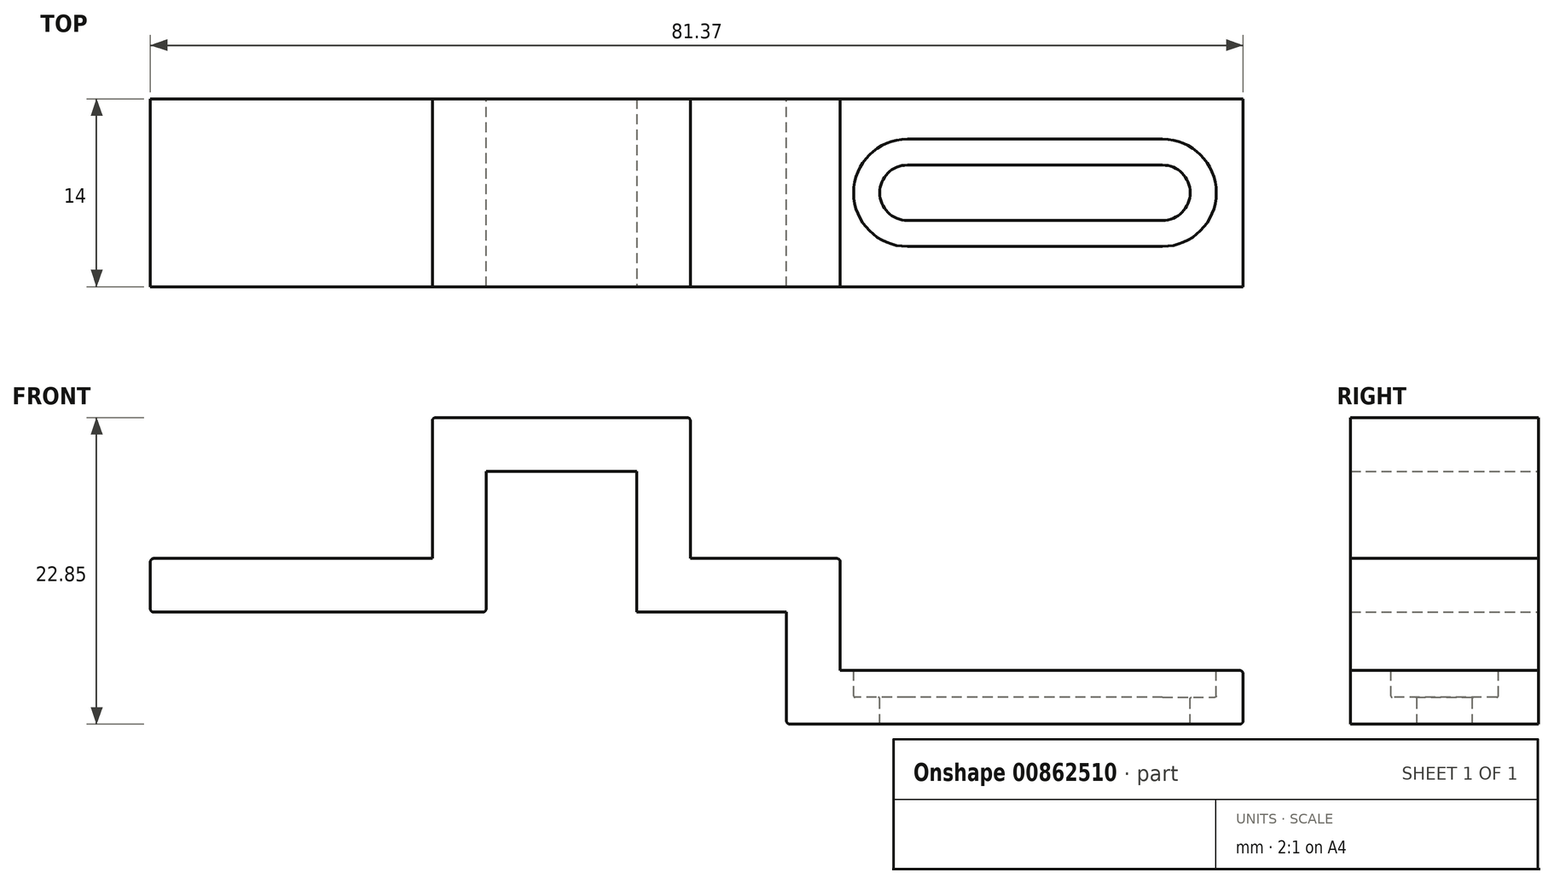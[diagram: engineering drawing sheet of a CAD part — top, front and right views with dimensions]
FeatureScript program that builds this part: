
annotation { "Feature Type Name" : "Feature", "Feature Type Description" : "" }
export const myFeature = defineFeature(function(context is Context, id is Id, definition is map)
    precondition{}
    {
        {
            var Q0;
            Q0=qCreatedBy(makeId("Right.planeOp"),FACE);
            var sketch = newSketch(context, id + "F0", { "sketchPlane" : qUnion([Q0])});
            skLineSegment(sketch, "E0.bottom", {"start": v(-7, -2) * mm, "end": v(7, -2) * mm});
            skLineSegment(sketch, "E0.top", {"start": v(-7, 2) * mm, "end": v(7, 2) * mm});
            skLineSegment(sketch, "E0.left", {"start": v(-7, -2) * mm, "end": v(-7, 2) * mm});
            skLineSegment(sketch, "E0.right", {"start": v(7, -2) * mm, "end": v(7, 2) * mm});
            skPoint(sketch, "E0.middle", {"position": v(0, 0) * mm});
            skSolve(sketch);
        }
        {
            var Q0;
            Q0 = qSketchRegion(id + "F0", true);
            extrude(context, id + "F1", {"entities" : qUnion([Q0]), "depth" : 25 * mm, "offsetDistance" : 25.4 * mm});
        }
        {
            var Q0;
            Q0=makeQuery(id+"F1.opExtrude","SWEPT_FACE",FACE,{"disambiguationData":[OSD([sQuery(id+"F0.wireOp",EDGE,"E0.top")])]});
            var sketch = newSketch(context, id + "F2", { "sketchPlane" : qUnion([Q0])});
            skLineSegment(sketch, "E1.bottom", {"start": v(25, -7) * mm, "end": v(21, -7) * mm});
            skLineSegment(sketch, "E1.top", {"start": v(25, 7) * mm, "end": v(21, 7) * mm});
            skLineSegment(sketch, "E1.left", {"start": v(25, -7) * mm, "end": v(25, 7) * mm});
            skLineSegment(sketch, "E1.right", {"start": v(21, -7) * mm, "end": v(21, 7) * mm});
            skSolve(sketch);
        }
        {
            var Q0;
            Q0 = qSketchRegion(id + "F2", true);
            extrude(context, id + "F3", {"entities" : qUnion([Q0]), "operationType" : NewBodyOperationType.ADD, "depth" : 10.5 * mm, "offsetDistance" : 25.4 * mm});
        }
        {
            var Q0;
            Q0=makeQuery(id+"F3.boolean.opBoolean","MERGE",FACE,{"derivedFrom":[makeQuery(id+"F1.opExtrude","CAP_FACE",FACE,{"disambiguationData":[OSD([sQuery(id+"F0.wireOp",EDGE,"E0.bottom"),sQuery(id+"F0.wireOp",EDGE,"E0.top"),sQuery(id+"F0.wireOp",EDGE,"E0.left"),sQuery(id+"F0.wireOp",EDGE,"E0.right")])],"isStart":false}),makeQuery(id+"F3.opExtrude","SWEPT_FACE",FACE,{"disambiguationData":[OSD([sQuery(id+"F2.wireOp",EDGE,"E1.left")])]})]});
            var sketch = newSketch(context, id + "F4", { "sketchPlane" : qUnion([Q0])});
            skLineSegment(sketch, "E2.bottom", {"start": v(-7, 12.5) * mm, "end": v(7, 12.5) * mm});
            skLineSegment(sketch, "E2.top", {"start": v(-7, 8.5) * mm, "end": v(7, 8.5) * mm});
            skLineSegment(sketch, "E2.left", {"start": v(-7, 12.5) * mm, "end": v(-7, 8.5) * mm});
            skLineSegment(sketch, "E2.right", {"start": v(7, 12.5) * mm, "end": v(7, 8.5) * mm});
            skSolve(sketch);
        }
        {
            var Q0;
            Q0 = qSketchRegion(id + "F4", true);
            extrude(context, id + "F5", {"entities" : qUnion([Q0]), "operationType" : NewBodyOperationType.ADD, "depth" : 15.21 * mm, "offsetDistance" : 25.4 * mm});
        }
        {
            var Q0;
            Q0=makeQuery(id+"F5.opExtrude","SWEPT_FACE",FACE,{"disambiguationData":[OSD([sQuery(id+"F4.wireOp",EDGE,"E2.top")])]});
            var sketch = newSketch(context, id + "F6", { "sketchPlane" : qUnion([Q0])});
            skLineSegment(sketch, "E3.bottom", {"start": v(40.21, 7) * mm, "end": v(36.21, 7) * mm});
            skLineSegment(sketch, "E3.top", {"start": v(40.21, -7) * mm, "end": v(36.21, -7) * mm});
            skLineSegment(sketch, "E3.left", {"start": v(40.21, 7) * mm, "end": v(40.21, -7) * mm});
            skLineSegment(sketch, "E3.right", {"start": v(36.21, 7) * mm, "end": v(36.21, -7) * mm});
            skSolve(sketch);
        }
        {
            var Q0;
            Q0 = qSketchRegion(id + "F6", true);
            var Q1;
            Q1=makeQuery(id+"F1.opExtrude","SWEPT_FACE",FACE,{"disambiguationData":[OSD([sQuery(id+"F0.wireOp",EDGE,"E0.bottom")])]});
            extrude(context, id + "F7", {"entities" : qUnion([Q0]), "operationType" : NewBodyOperationType.ADD, "endBound" : BoundingType.UP_TO_SURFACE, "depth" : 25.4 * mm, "endBoundEntityFace" : qUnion([Q1]), "offsetDistance" : 25.4 * mm});
        }
        {
            var Q0;
            Q0=makeQuery(id+"F7.boolean.opBoolean","MERGE",FACE,{"derivedFrom":[makeQuery(id+"F5.opExtrude","CAP_FACE",FACE,{"disambiguationData":[OSD([sQuery(id+"F4.wireOp",EDGE,"E2.bottom"),sQuery(id+"F4.wireOp",EDGE,"E2.top"),sQuery(id+"F4.wireOp",EDGE,"E2.left"),sQuery(id+"F4.wireOp",EDGE,"E2.right")])],"isStart":false}),makeQuery(id+"F7.opExtrude","SWEPT_FACE",FACE,{"disambiguationData":[OSD([sQuery(id+"F6.wireOp",EDGE,"E3.left")])]})]});
            var sketch = newSketch(context, id + "F8", { "sketchPlane" : qUnion([Q0])});
            skLineSegment(sketch, "E4.bottom", {"start": v(-7, -2) * mm, "end": v(7, -2) * mm});
            skLineSegment(sketch, "E4.top", {"start": v(-7, 2) * mm, "end": v(7, 2) * mm});
            skLineSegment(sketch, "E4.left", {"start": v(-7, -2) * mm, "end": v(-7, 2) * mm});
            skLineSegment(sketch, "E4.right", {"start": v(7, -2) * mm, "end": v(7, 2) * mm});
            skSolve(sketch);
        }
        {
            var Q0;
            Q0 = qSketchRegion(id + "F8", true);
            extrude(context, id + "F9", {"entities" : qUnion([Q0]), "operationType" : NewBodyOperationType.ADD, "depth" : 11.16 * mm, "offsetDistance" : 25.4 * mm});
        }
        {
            var Q0;
            Q0=makeQuery(id+"F9.boolean.opBoolean","MERGE",FACE,{"derivedFrom":[makeQuery(id+"F7.opExtrude","CAP_FACE",FACE,{"disambiguationData":[OSD([sQuery(id+"F0.wireOp",EDGE,"E0.bottom")])],"isStart":false}),makeQuery(id+"F9.opExtrude","SWEPT_FACE",FACE,{"disambiguationData":[OSD([sQuery(id+"F8.wireOp",EDGE,"E4.bottom")])]})]});
            var sketch = newSketch(context, id + "F10", { "sketchPlane" : qUnion([Q0])});
            skLineSegment(sketch, "E5.bottom", {"start": v(51.37, 7) * mm, "end": v(47.37, 7) * mm});
            skLineSegment(sketch, "E5.top", {"start": v(51.37, -7) * mm, "end": v(47.37, -7) * mm});
            skLineSegment(sketch, "E5.left", {"start": v(51.37, 7) * mm, "end": v(51.37, -7) * mm});
            skLineSegment(sketch, "E5.right", {"start": v(47.37, 7) * mm, "end": v(47.37, -7) * mm});
            skSolve(sketch);
        }
        {
            var Q0;
            Q0 = qSketchRegion(id + "F10", true);
            extrude(context, id + "F11", {"entities" : qUnion([Q0]), "operationType" : NewBodyOperationType.ADD, "depth" : 8.35 * mm, "offsetDistance" : 25.4 * mm});
        }
        {
            var Q0;
            Q0=makeQuery(id+"F11.boolean.opBoolean","MERGE",FACE,{"derivedFrom":[makeQuery(id+"F9.opExtrude","CAP_FACE",FACE,{"disambiguationData":[OSD([sQuery(id+"F8.wireOp",EDGE,"E4.bottom"),sQuery(id+"F8.wireOp",EDGE,"E4.top"),sQuery(id+"F8.wireOp",EDGE,"E4.left"),sQuery(id+"F8.wireOp",EDGE,"E4.right")])],"isStart":false}),makeQuery(id+"F11.opExtrude","SWEPT_FACE",FACE,{"disambiguationData":[OSD([sQuery(id+"F10.wireOp",EDGE,"E5.left")])]})]});
            var sketch = newSketch(context, id + "F12", { "sketchPlane" : qUnion([Q0])});
            skLineSegment(sketch, "E6.bottom", {"start": v(7, -10.35) * mm, "end": v(-7, -10.35) * mm});
            skLineSegment(sketch, "E6.top", {"start": v(7, -6.35) * mm, "end": v(-7, -6.35) * mm});
            skLineSegment(sketch, "E6.left", {"start": v(7, -10.35) * mm, "end": v(7, -6.35) * mm});
            skLineSegment(sketch, "E6.right", {"start": v(-7, -10.35) * mm, "end": v(-7, -6.35) * mm});
            skSolve(sketch);
        }
        {
            var Q0;
            Q0 = qSketchRegion(id + "F12", true);
            extrude(context, id + "F13", {"entities" : qUnion([Q0]), "operationType" : NewBodyOperationType.ADD, "depth" : 30 * mm, "offsetDistance" : 25.4 * mm});
        }
        {
            var Q0;
            Q0=makeQuery(id+"F13.opExtrude","SWEPT_FACE",FACE,{"disambiguationData":[OSD([sQuery(id+"F12.wireOp",EDGE,"E6.top")])]});
            var sketch = newSketch(context, id + "F14", { "sketchPlane" : qUnion([Q0])});
            skLineSegment(sketch, "E7.bottom", {"start": v(51.37, 7) * mm, "end": v(81.37, 7) * mm, "construction": true});
            skLineSegment(sketch, "E7.top", {"start": v(51.37, 0) * mm, "end": v(81.37, 0) * mm, "construction": true});
            skLineSegment(sketch, "E7.left", {"start": v(51.37, 7) * mm, "end": v(51.37, 0) * mm, "construction": true});
            skLineSegment(sketch, "E7.right", {"start": v(81.37, 7) * mm, "end": v(81.37, 0) * mm, "construction": true});
            skCircle(sketch, "E8", {"center": v(56.37, 0) * mm, "radius": 2.06 * mm});
            skCircle(sketch, "E9", {"center": v(75.37, 0) * mm, "radius": 2.06 * mm});
            skLineSegment(sketch, "E10", {"start": v(56.37, 2.06) * mm, "end": v(75.37, 2.06) * mm});
            skLineSegment(sketch, "E11", {"start": v(56.37, -2.06) * mm, "end": v(75.37, -2.06) * mm});
            skSolve(sketch);
        }
        {
            var Q0;
            Q0 = qSketchRegion(id + "F14", true);
            var Q1;
            Q1=makeQuery(id+"F13.boolean.opBoolean","MERGE",FACE,{"derivedFrom":[makeQuery(id+"F11.opExtrude","CAP_FACE",FACE,{"disambiguationData":[OSD([sQuery(id+"F10.wireOp",EDGE,"E5.bottom"),sQuery(id+"F10.wireOp",EDGE,"E5.top"),sQuery(id+"F10.wireOp",EDGE,"E5.left"),sQuery(id+"F10.wireOp",EDGE,"E5.right")])],"isStart":false}),makeQuery(id+"F13.opExtrude","SWEPT_FACE",FACE,{"disambiguationData":[OSD([sQuery(id+"F12.wireOp",EDGE,"E6.bottom")])]})]});
            extrude(context, id + "F15", {"entities" : qUnion([Q0]), "operationType" : NewBodyOperationType.REMOVE, "endBound" : BoundingType.UP_TO_SURFACE, "oppositeDirection" : true, "depth" : 25.4 * mm, "endBoundEntityFace" : qUnion([Q1]), "offsetDistance" : 25.4 * mm});
        }
        {
            var Q0;
            Q0=makeQuery(id+"F13.opExtrude","SWEPT_FACE",FACE,{"disambiguationData":[OSD([sQuery(id+"F12.wireOp",EDGE,"E6.top")])]});
            var sketch = newSketch(context, id + "F16", { "sketchPlane" : qUnion([Q0])});
            skLineSegment(sketch, "E12.bottom", {"start": v(81.37, 7) * mm, "end": v(51.37, 7) * mm, "construction": true});
            skLineSegment(sketch, "E12.top", {"start": v(81.37, 0) * mm, "end": v(51.37, 0) * mm, "construction": true});
            skLineSegment(sketch, "E12.left", {"start": v(81.37, 7) * mm, "end": v(81.37, 0) * mm, "construction": true});
            skLineSegment(sketch, "E12.right", {"start": v(51.37, 7) * mm, "end": v(51.37, 0) * mm, "construction": true});
            skCircle(sketch, "E13", {"center": v(56.37, 0) * mm, "radius": 4 * mm});
            skCircle(sketch, "E14", {"center": v(75.37, 0) * mm, "radius": 4 * mm});
            skLineSegment(sketch, "E15", {"start": v(56.37, 4) * mm, "end": v(75.37, 4) * mm});
            skLineSegment(sketch, "E16", {"start": v(56.37, -4) * mm, "end": v(75.37, -4) * mm});
            skSolve(sketch);
        }
        {
            var Q0;
            Q0 = qSketchRegion(id + "F16", true);
            extrude(context, id + "F17", {"entities" : qUnion([Q0]), "operationType" : NewBodyOperationType.REMOVE, "oppositeDirection" : true, "depth" : 2 * mm, "offsetDistance" : 25.4 * mm});
        }
        {
            var Q0;
            Q0=makeQuery(id+"F17.boolean.opBoolean","COPY",EDGE,{"derivedFrom":makeQuery(id+"F17.opExtrude","CAP_EDGE",EDGE,{"disambiguationData":[OSD([sQuery(id+"F16.wireOp",EDGE,"E13")])],"isStart":true})});
            var Q1;
            Q1=makeQuery(id+"F17.boolean.opBoolean","COPY",EDGE,{"derivedFrom":makeQuery(id+"F17.opExtrude","CAP_EDGE",EDGE,{"disambiguationData":[OSD([sQuery(id+"F16.wireOp",EDGE,"E15")])],"isStart":true})});
            var Q2;
            Q2=makeQuery(id+"F17.boolean.opBoolean","COPY",EDGE,{"derivedFrom":makeQuery(id+"F17.opExtrude","CAP_EDGE",EDGE,{"disambiguationData":[OSD([sQuery(id+"F16.wireOp",EDGE,"E14")])],"isStart":true})});
            var Q3;
            Q3=makeQuery(id+"F17.boolean.opBoolean","COPY",EDGE,{"derivedFrom":makeQuery(id+"F17.opExtrude","CAP_EDGE",EDGE,{"disambiguationData":[OSD([sQuery(id+"F16.wireOp",EDGE,"E16")])],"isStart":true})});
            var Q4;
            Q4=makeQuery(id+"F17.boolean.opBoolean","COPY",EDGE,{"derivedFrom":makeQuery(id+"F17.opExtrude","CAP_EDGE",EDGE,{"disambiguationData":[OSD([sQuery(id+"F16.wireOp",EDGE,"E15")])],"isStart":false})});
            var Q5;
            Q5=makeQuery(id+"F17.boolean.opBoolean","COPY",EDGE,{"derivedFrom":makeQuery(id+"F17.opExtrude","CAP_EDGE",EDGE,{"disambiguationData":[OSD([sQuery(id+"F16.wireOp",EDGE,"E13")])],"isStart":false})});
            var Q6;
            Q6=makeQuery(id+"F17.boolean.opBoolean","INTERSECT",EDGE,{"derivedFrom":[makeQuery(id+"F15.boolean.opBoolean","COPY",FACE,{"derivedFrom":makeQuery(id+"F15.opExtrude","SWEPT_FACE",FACE,{"disambiguationData":[OSD([sQuery(id+"F14.wireOp",EDGE,"E8")])]})}),makeQuery(id+"F17.opExtrude","CAP_FACE",FACE,{"disambiguationData":[OSD([sQuery(id+"F16.wireOp",EDGE,"E13"),sQuery(id+"F16.wireOp",EDGE,"E14"),sQuery(id+"F16.wireOp",EDGE,"E15"),sQuery(id+"F16.wireOp",EDGE,"E16")])],"isStart":false})]});
            var Q7;
            Q7=makeQuery(id+"F17.boolean.opBoolean","INTERSECT",EDGE,{"derivedFrom":[makeQuery(id+"F15.boolean.opBoolean","COPY",FACE,{"derivedFrom":makeQuery(id+"F15.opExtrude","SWEPT_FACE",FACE,{"disambiguationData":[OSD([sQuery(id+"F14.wireOp",EDGE,"E10")])]})}),makeQuery(id+"F17.opExtrude","CAP_FACE",FACE,{"disambiguationData":[OSD([sQuery(id+"F16.wireOp",EDGE,"E13"),sQuery(id+"F16.wireOp",EDGE,"E14"),sQuery(id+"F16.wireOp",EDGE,"E15"),sQuery(id+"F16.wireOp",EDGE,"E16")])],"isStart":false})]});
            var Q8;
            Q8=makeQuery(id+"F17.boolean.opBoolean","INTERSECT",EDGE,{"derivedFrom":[makeQuery(id+"F15.boolean.opBoolean","COPY",FACE,{"derivedFrom":makeQuery(id+"F15.opExtrude","SWEPT_FACE",FACE,{"disambiguationData":[OSD([sQuery(id+"F14.wireOp",EDGE,"E9")])]})}),makeQuery(id+"F17.opExtrude","CAP_FACE",FACE,{"disambiguationData":[OSD([sQuery(id+"F16.wireOp",EDGE,"E13"),sQuery(id+"F16.wireOp",EDGE,"E14"),sQuery(id+"F16.wireOp",EDGE,"E15"),sQuery(id+"F16.wireOp",EDGE,"E16")])],"isStart":false})]});
            var Q9;
            Q9=makeQuery(id+"F17.boolean.opBoolean","COPY",EDGE,{"derivedFrom":makeQuery(id+"F17.opExtrude","CAP_EDGE",EDGE,{"disambiguationData":[OSD([sQuery(id+"F16.wireOp",EDGE,"E14")])],"isStart":false})});
            var Q10;
            Q10=makeQuery(id+"F17.boolean.opBoolean","COPY",EDGE,{"derivedFrom":makeQuery(id+"F17.opExtrude","CAP_EDGE",EDGE,{"disambiguationData":[OSD([sQuery(id+"F16.wireOp",EDGE,"E16")])],"isStart":false})});
            var Q11;
            Q11=makeQuery(id+"F17.boolean.opBoolean","INTERSECT",EDGE,{"derivedFrom":[makeQuery(id+"F15.boolean.opBoolean","COPY",FACE,{"derivedFrom":makeQuery(id+"F15.opExtrude","SWEPT_FACE",FACE,{"disambiguationData":[OSD([sQuery(id+"F14.wireOp",EDGE,"E11")])]})}),makeQuery(id+"F17.opExtrude","CAP_FACE",FACE,{"disambiguationData":[OSD([sQuery(id+"F16.wireOp",EDGE,"E13"),sQuery(id+"F16.wireOp",EDGE,"E14"),sQuery(id+"F16.wireOp",EDGE,"E15"),sQuery(id+"F16.wireOp",EDGE,"E16")])],"isStart":false})]});
            fillet(context, id + "F18", {"entities" : qUnion([Q0, Q1, Q2, Q3, Q4, Q5, Q6, Q7, Q8, Q9, Q10, Q11]), "radius" : 0.1 * mm, "tangentPropagation" : true, "allowEdgeOverflow" : false});
        }
        {
            var Q0;
            Q0=makeQuery(id+"F13.opExtrude","CAP_EDGE",EDGE,{"disambiguationData":[OSD([sQuery(id+"F12.wireOp",EDGE,"E6.top")])],"isStart":true});
            var Q1;
            Q1=makeQuery(id+"F9.opExtrude","CAP_EDGE",EDGE,{"disambiguationData":[OSD([sQuery(id+"F8.wireOp",EDGE,"E4.top")])],"isStart":false});
            var Q2;
            Q2=makeQuery(id+"F9.opExtrude","CAP_EDGE",EDGE,{"disambiguationData":[OSD([sQuery(id+"F8.wireOp",EDGE,"E4.top")])],"isStart":true});
            var Q3;
            Q3=makeQuery(id+"F5.opExtrude","CAP_EDGE",EDGE,{"disambiguationData":[OSD([sQuery(id+"F4.wireOp",EDGE,"E2.bottom")])],"isStart":false});
            var Q4;
            Q4=makeQuery(id+"F3.opExtrude","CAP_EDGE",EDGE,{"disambiguationData":[OSD([sQuery(id+"F2.wireOp",EDGE,"E1.right")])],"isStart":true});
            var Q5;
            Q5=makeQuery(id+"F3.opExtrude","CAP_EDGE",EDGE,{"disambiguationData":[OSD([sQuery(id+"F2.wireOp",EDGE,"E1.right")])],"isStart":false});
            var Q6;
            Q6=makeQuery(id+"F1.opExtrude","CAP_EDGE",EDGE,{"disambiguationData":[OSD([sQuery(id+"F0.wireOp",EDGE,"E0.top")])],"isStart":true});
            var Q7;
            Q7=makeQuery(id+"F1.opExtrude","CAP_EDGE",EDGE,{"disambiguationData":[OSD([sQuery(id+"F0.wireOp",EDGE,"E0.bottom")])],"isStart":true});
            var Q8;
            Q8=makeQuery(id+"F1.opExtrude","CAP_EDGE",EDGE,{"disambiguationData":[OSD([sQuery(id+"F0.wireOp",EDGE,"E0.bottom")])],"isStart":false});
            var Q9;
            Q9=makeQuery(id+"F5.opExtrude","CAP_EDGE",EDGE,{"disambiguationData":[OSD([sQuery(id+"F4.wireOp",EDGE,"E2.top")])],"isStart":true});
            var Q10;
            Q10=makeQuery(id+"F7.opExtrude","CAP_EDGE",EDGE,{"disambiguationData":[OSD([sQuery(id+"F6.wireOp",EDGE,"E3.right")])],"isStart":true});
            var Q11;
            Q11=makeQuery(id+"F7.opExtrude","TWEAK_EDGE",EDGE,{"derivedFrom":[makeQuery(id+"F1.opExtrude","SWEPT_FACE",FACE,{"disambiguationData":[OSD([sQuery(id+"F0.wireOp",EDGE,"E0.bottom")])]}),makeQuery(id+"F6.imprint","IMPRINT",EDGE,{"derivedFrom":sQuery(id+"F6.wireOp",EDGE,"E3.right")})]});
            var Q12;
            Q12=makeQuery(id+"F11.opExtrude","CAP_EDGE",EDGE,{"disambiguationData":[OSD([sQuery(id+"F10.wireOp",EDGE,"E5.right")])],"isStart":true});
            var Q13;
            Q13=makeQuery(id+"F11.opExtrude","CAP_EDGE",EDGE,{"disambiguationData":[OSD([sQuery(id+"F10.wireOp",EDGE,"E5.right")])],"isStart":false});
            var Q14;
            Q14=makeQuery(id+"F13.opExtrude","CAP_EDGE",EDGE,{"disambiguationData":[OSD([sQuery(id+"F12.wireOp",EDGE,"E6.bottom")])],"isStart":false});
            var Q15;
            Q15=makeQuery(id+"F13.opExtrude","CAP_EDGE",EDGE,{"disambiguationData":[OSD([sQuery(id+"F12.wireOp",EDGE,"E6.top")])],"isStart":false});
            fillet(context, id + "F19", {"entities" : qUnion([Q0, Q1, Q2, Q3, Q4, Q5, Q6, Q7, Q8, Q9, Q10, Q11, Q12, Q13, Q14, Q15]), "radius" : 0.25 * mm, "tangentPropagation" : true, "allowEdgeOverflow" : false});
        }
    });
